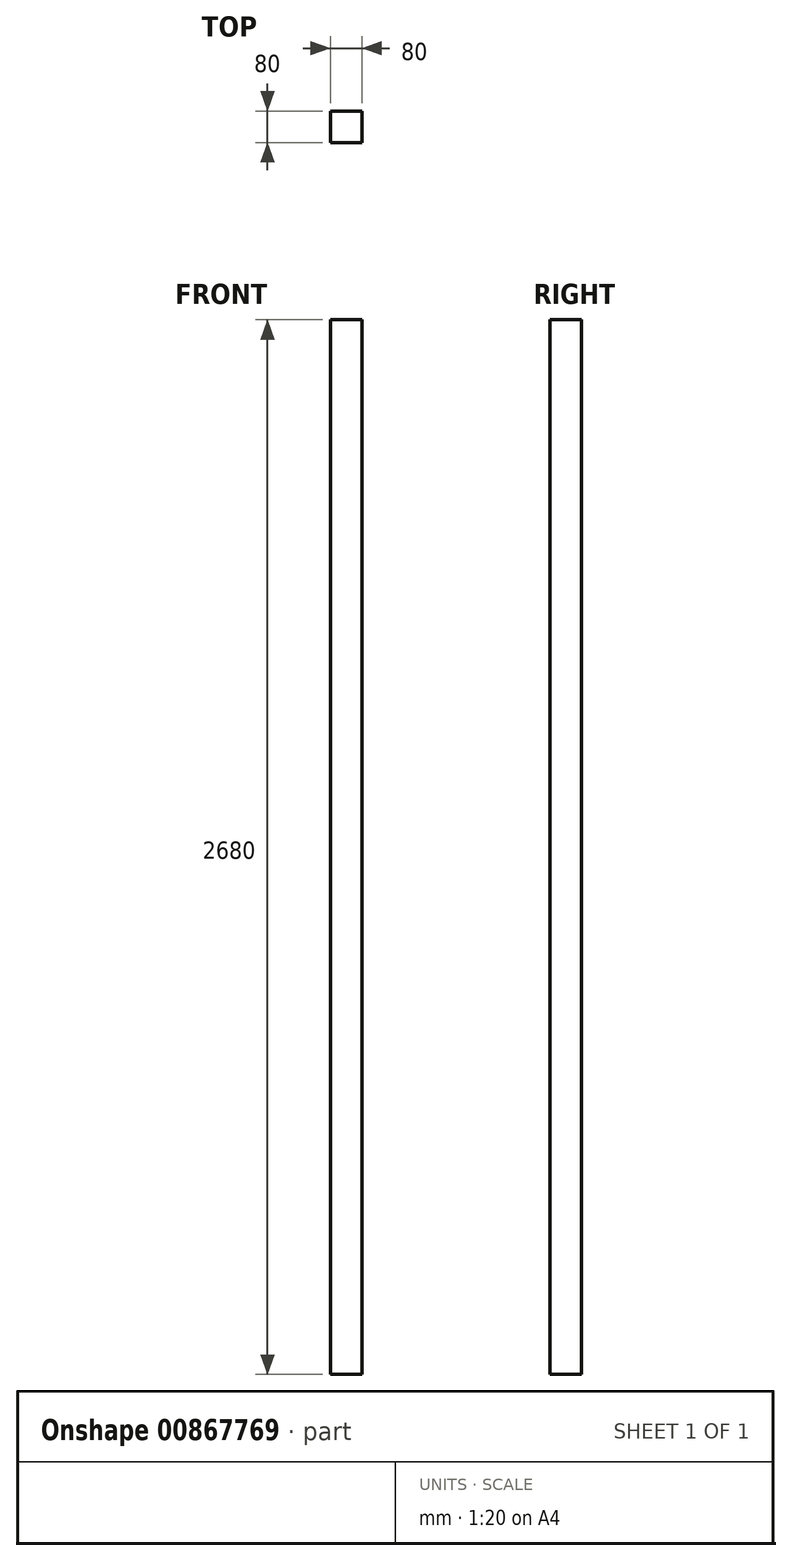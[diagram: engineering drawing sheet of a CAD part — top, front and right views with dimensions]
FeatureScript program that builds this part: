
annotation { "Feature Type Name" : "Feature", "Feature Type Description" : "" }
export const myFeature = defineFeature(function(context is Context, id is Id, definition is map)
    precondition{}
    {
        {
            var Q0;
            Q0=qCreatedBy(makeId("Top.planeOp"),FACE);
            var sketch = newSketch(context, id + "F0", { "sketchPlane" : qUnion([Q0])});
            skLineSegment(sketch, "E0.bottom", {"start": v(40, -40) * mm, "end": v(-40, -40) * mm});
            skLineSegment(sketch, "E0.top", {"start": v(40, 40) * mm, "end": v(-40, 40) * mm});
            skLineSegment(sketch, "E0.left", {"start": v(40, -40) * mm, "end": v(40, 40) * mm});
            skLineSegment(sketch, "E0.right", {"start": v(-40, -40) * mm, "end": v(-40, 40) * mm});
            skPoint(sketch, "E0.middle", {"position": v(0, 0) * mm});
            skSolve(sketch);
        }
        {
            var Q0;
            Q0=makeQuery(id+"F0.imprint","IMPRINT",FACE,{"disambiguationData":[TD([[makeQuery(id+"F0.imprint","IMPRINT",EDGE,{"derivedFrom":sQuery(id+"F0.wireOp",EDGE,"E0.bottom")}),-1.0]])]});
            extrude(context, id + "F1", {"entities" : qUnion([Q0]), "depth" : 2680 * mm, "offsetDistance" : 25 * mm});
        }
    });
